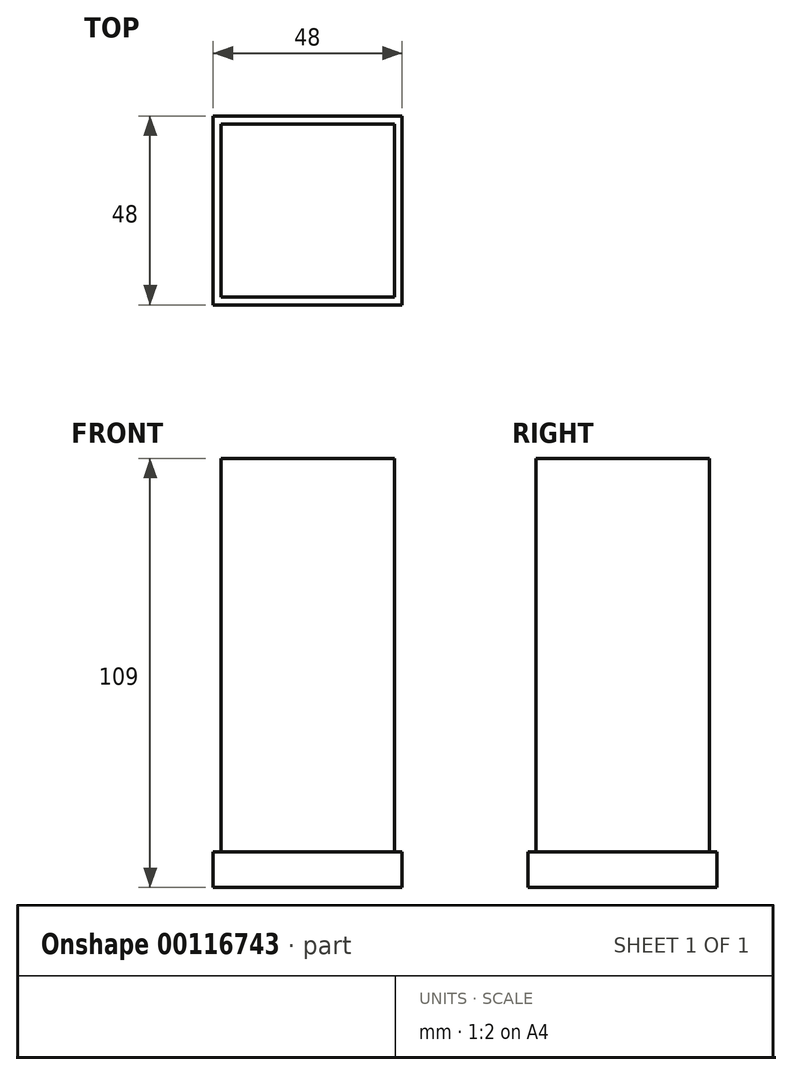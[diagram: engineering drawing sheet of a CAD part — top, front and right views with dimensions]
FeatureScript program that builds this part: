
annotation { "Feature Type Name" : "Feature", "Feature Type Description" : "" }
export const myFeature = defineFeature(function(context is Context, id is Id, definition is map)
    precondition{}
    {
        {
            var Q0;
            Q0=qCreatedBy(makeId("Top.planeOp"),FACE);
            var sketch = newSketch(context, id + "F0", { "sketchPlane" : qUnion([Q0])});
            skLineSegment(sketch, "E0.bottom", {"start": v(22, 22) * mm, "end": v(-22, 22) * mm});
            skLineSegment(sketch, "E0.top", {"start": v(22, -22) * mm, "end": v(-22, -22) * mm});
            skLineSegment(sketch, "E0.left", {"start": v(22, 22) * mm, "end": v(22, -22) * mm});
            skLineSegment(sketch, "E0.right", {"start": v(-22, 22) * mm, "end": v(-22, -22) * mm});
            skPoint(sketch, "E0.middle", {"position": v(0, 0) * mm});
            skSolve(sketch);
        }
        {
            var Q0;
            Q0 = qSketchRegion(id + "F0", true);
            extrude(context, id + "F1", {"entities" : qUnion([Q0]), "depth" : 100 * mm});
        }
        {
            var Q0;
            Q0=qCreatedBy(makeId("Top.planeOp"),FACE);
            var sketch = newSketch(context, id + "F2", { "sketchPlane" : qUnion([Q0])});
            skLineSegment(sketch, "E1.bottom", {"start": v(-24, -24) * mm, "end": v(24, -24) * mm});
            skLineSegment(sketch, "E1.top", {"start": v(-24, 24) * mm, "end": v(24, 24) * mm});
            skLineSegment(sketch, "E1.left", {"start": v(-24, -24) * mm, "end": v(-24, 24) * mm});
            skLineSegment(sketch, "E1.right", {"start": v(24, -24) * mm, "end": v(24, 24) * mm});
            skPoint(sketch, "E1.middle", {"position": v(0, 0) * mm});
            skSolve(sketch);
        }
        {
            var Q0;
            Q0 = qSketchRegion(id + "F2", true);
            extrude(context, id + "F3", {"entities" : qUnion([Q0]), "oppositeDirection" : true, "depth" : 9 * mm});
        }
    });
